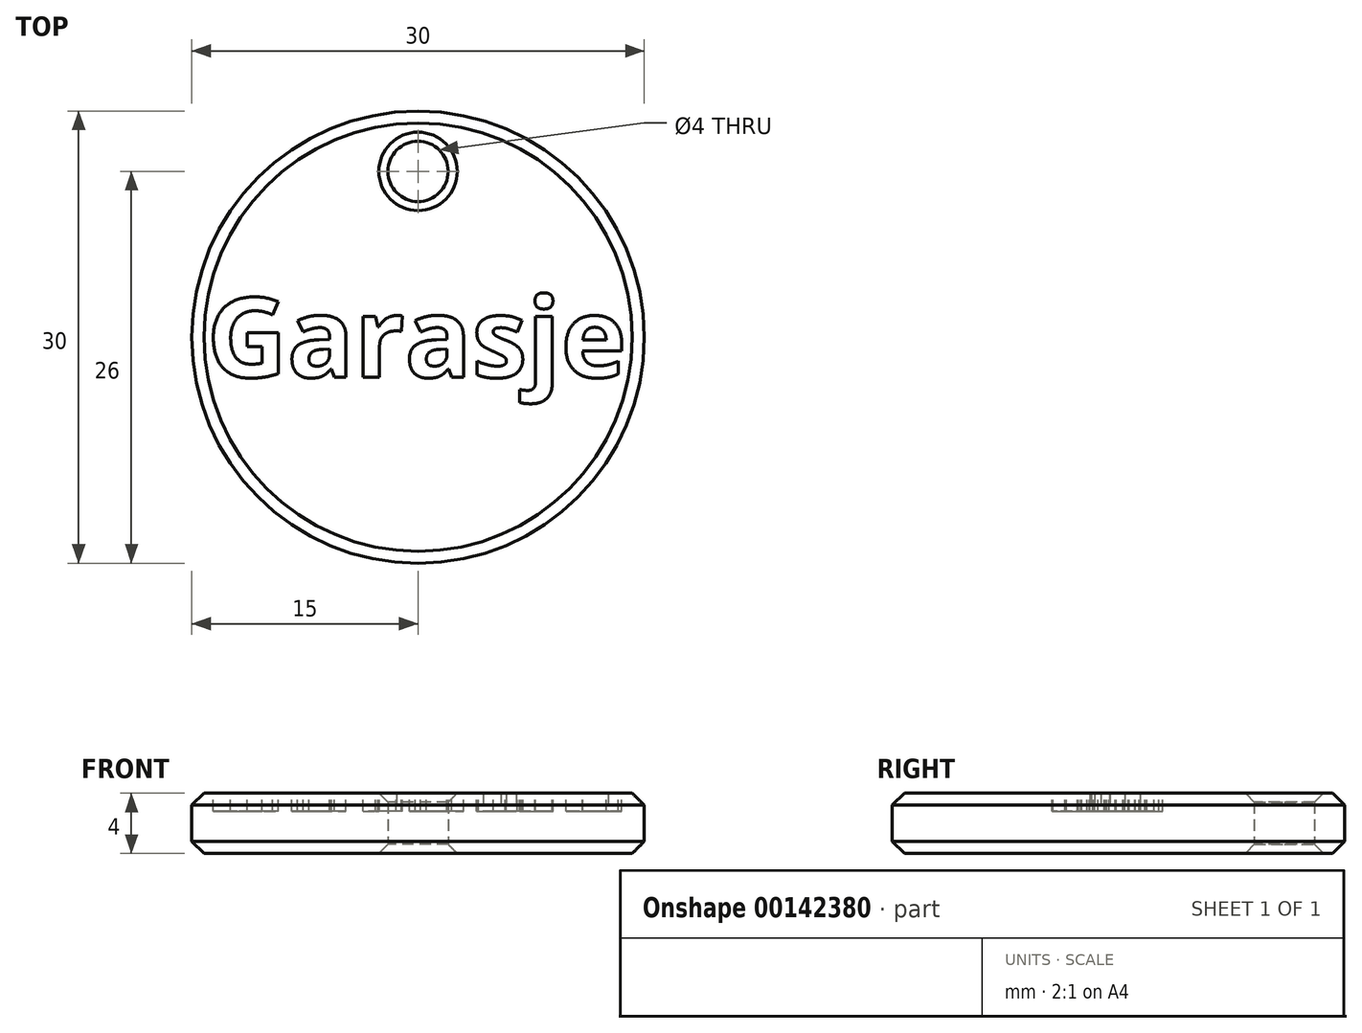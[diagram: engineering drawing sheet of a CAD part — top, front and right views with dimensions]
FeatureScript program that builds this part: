
annotation { "Feature Type Name" : "Feature", "Feature Type Description" : "" }
export const myFeature = defineFeature(function(context is Context, id is Id, definition is map)
    precondition{}
    {
        {
            var Q0;
            Q0=qCreatedBy(makeId("Top.planeOp"),FACE);
            var sketch = newSketch(context, id + "F0", { "sketchPlane" : qUnion([Q0])});
            skCircle(sketch, "E0", {"center": v(0, 0) * mm, "radius": 15 * mm});
            skCircle(sketch, "E1", {"center": v(0, 11) * mm, "radius": 2 * mm});
            skSolve(sketch);
        }
        {
            var Q0;
            Q0=makeQuery(id+"F0.imprint","IMPRINT",FACE,{"disambiguationData":[TD([[makeQuery(id+"F0.imprint","IMPRINT",EDGE,{"derivedFrom":sQuery(id+"F0.wireOp",EDGE,"E0")}),1.0]])]});
            extrude(context, id + "F1", {"entities" : qUnion([Q0]), "depth" : 4 * mm});
        }
        {
            var Q0;
            Q0=makeQuery(id+"F1.opExtrude","CAP_FACE",FACE,{"disambiguationData":[OSD([sQuery(id+"F0.wireOp",EDGE,"E0"),sQuery(id+"F0.wireOp",EDGE,"E1")])],"isStart":false});
            var sketch = newSketch(context, id + "F2", { "sketchPlane" : qUnion([Q0])});
            skText(sketch, "E2", { "text": "Garasje", "fontName": "OpenSans-Bold.ttf"});
            skPoint(sketch, "E3", {"position": v(0, 0) * mm});
            const initialGuessF2  = {"E2": [-0.014, -0.00265, 1, 0, 0.0053]};
            skSetInitialGuess(sketch, initialGuessF2);
            skSolve(sketch);
        }
        {
            var Q0;
            Q0 = qSketchRegion(id + "F2", true);
            extrude(context, id + "F3", {"entities" : qUnion([Q0]), "operationType" : NewBodyOperationType.REMOVE, "oppositeDirection" : true, "depth" : 1.2 * mm});
        }
        {
            var Q0;
            Q0=makeQuery(id+"F1.opExtrude","CAP_EDGE",EDGE,{"disambiguationData":[OSD([sQuery(id+"F0.wireOp",EDGE,"E0")])],"isStart":false});
            var Q1;
            Q1=makeQuery(id+"F1.opExtrude","CAP_EDGE",EDGE,{"disambiguationData":[OSD([sQuery(id+"F0.wireOp",EDGE,"E0")])],"isStart":true});
            chamfer(context, id + "F4", {"entities" : qUnion([Q0, Q1]), "width" : 0.8 * mm, "tangentPropagation" : true});
        }
        {
            var Q0;
            Q0=makeQuery(id+"F1.opExtrude","CAP_EDGE",EDGE,{"disambiguationData":[OSD([sQuery(id+"F0.wireOp",EDGE,"E1")])],"isStart":false});
            var Q1;
            Q1=makeQuery(id+"F1.opExtrude","CAP_EDGE",EDGE,{"disambiguationData":[OSD([sQuery(id+"F0.wireOp",EDGE,"E1")])],"isStart":true});
            chamfer(context, id + "F5", {"entities" : qUnion([Q0, Q1]), "width" : 0.6 * mm, "tangentPropagation" : true});
        }
    });
